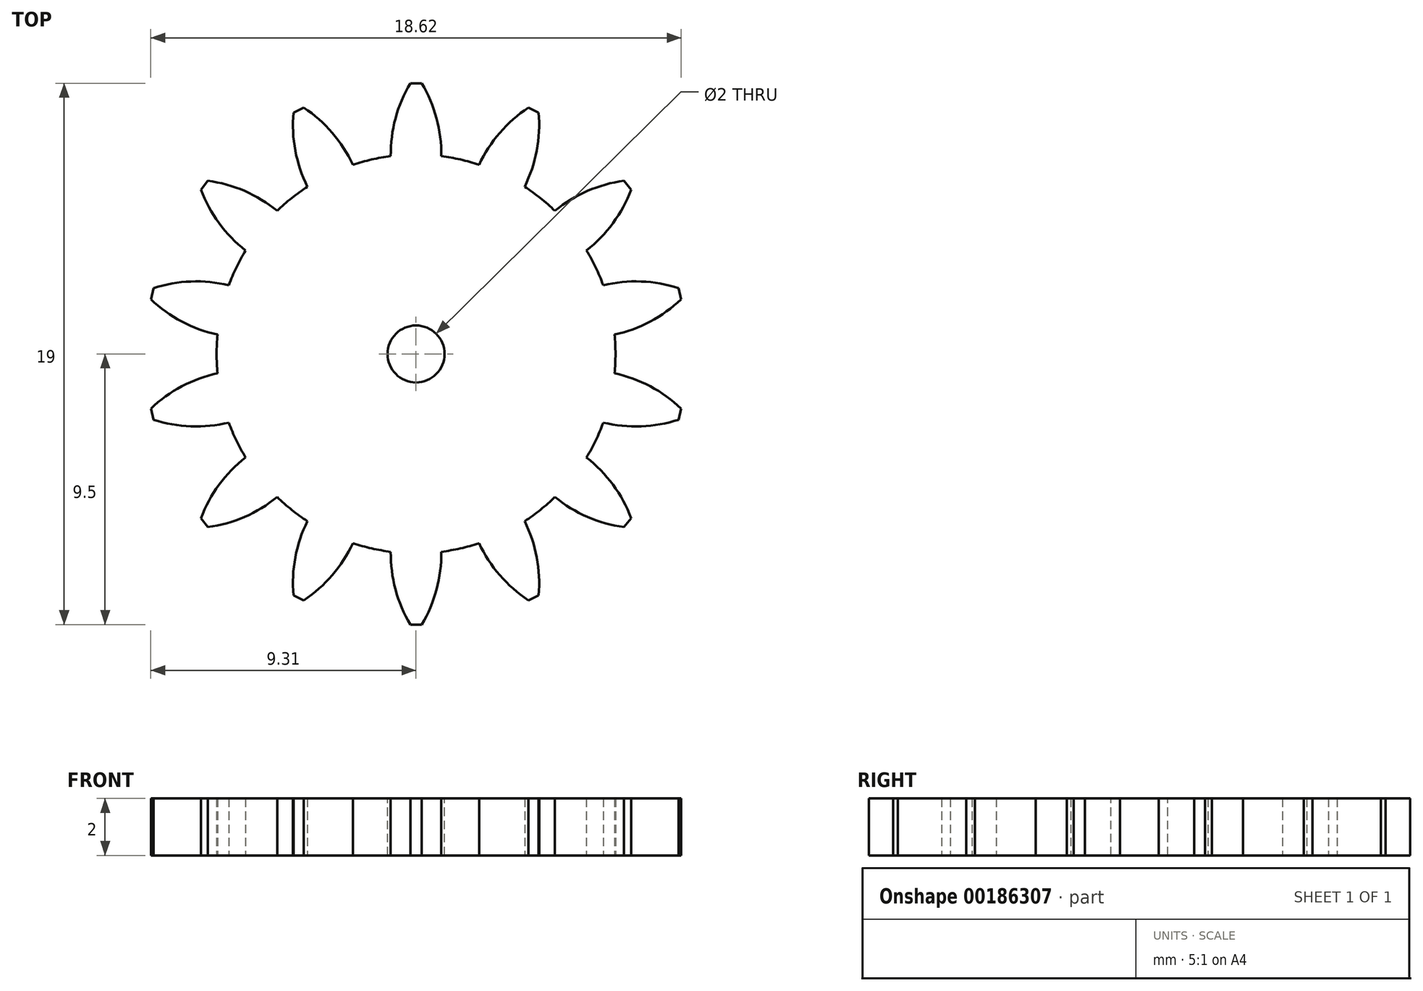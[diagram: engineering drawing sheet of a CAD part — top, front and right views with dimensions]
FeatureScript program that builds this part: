
annotation { "Feature Type Name" : "Feature", "Feature Type Description" : "" }
export const myFeature = defineFeature(function(context is Context, id is Id, definition is map)
    precondition{}
    {
        {
            var Q0;
            Q0=qCreatedBy(makeId("Top.planeOp"),FACE);
            var sketch = newSketch(context, id + "F0", { "sketchPlane" : qUnion([Q0])});
            skCircle(sketch, "E0", {"center": v(0, 0) * mm, "radius": 7 * mm});
            skLineSegment(sketch, "E1", {"start": v(0, 0) * mm, "end": v(0, 7) * mm, "construction": true});
            skArc(sketch, "E2", {"start": v(-0.2, 9.5) * mm, "mid": v(-0.72, 8.27) * mm, "end": v(-0.89, 6.94) * mm});
            skLineSegment(sketch, "E3", {"start": v(0, 9.5) * mm, "end": v(-0.2, 9.5) * mm});
            skLineSegment(sketch, "E4.MirrorCS", {"start": v(0, 9.5) * mm, "end": v(0.2, 9.5) * mm});
            skArc(sketch, "E5.MirrorCS", {"start": v(0.2, 9.5) * mm, "mid": v(0.72, 8.27) * mm, "end": v(0.89, 6.94) * mm});
            skArc(sketch, "E6.1.0", {"start": v(-3.94, 8.65) * mm, "mid": v(-2.94, 7.76) * mm, "end": v(-2.21, 6.64) * mm});
            skLineSegment(sketch, "E6.1.1", {"start": v(-4.12, 8.56) * mm, "end": v(-3.94, 8.65) * mm});
            skLineSegment(sketch, "E6.1.2", {"start": v(-4.12, 8.56) * mm, "end": v(-4.3, 8.47) * mm});
            skArc(sketch, "E6.1.3", {"start": v(-4.3, 8.47) * mm, "mid": v(-4.24, 7.14) * mm, "end": v(-3.81, 5.87) * mm});
            skArc(sketch, "E6.2.0", {"start": v(-7.3, 6.08) * mm, "mid": v(-6.02, 5.72) * mm, "end": v(-4.88, 5.02) * mm});
            skLineSegment(sketch, "E6.2.1", {"start": v(-7.43, 5.92) * mm, "end": v(-7.3, 6.08) * mm});
            skLineSegment(sketch, "E6.2.2", {"start": v(-7.43, 5.92) * mm, "end": v(-7.55, 5.77) * mm});
            skArc(sketch, "E6.2.3", {"start": v(-7.55, 5.77) * mm, "mid": v(-6.91, 4.6) * mm, "end": v(-5.98, 3.64) * mm});
            skArc(sketch, "E6.3.0", {"start": v(-9.22, 2.3) * mm, "mid": v(-7.9, 2.54) * mm, "end": v(-6.57, 2.41) * mm});
            skLineSegment(sketch, "E6.3.1", {"start": v(-9.26, 2.11) * mm, "end": v(-9.22, 2.3) * mm});
            skLineSegment(sketch, "E6.3.2", {"start": v(-9.26, 2.11) * mm, "end": v(-9.3, 1.92) * mm});
            skArc(sketch, "E6.3.3", {"start": v(-9.3, 1.92) * mm, "mid": v(-8.22, 1.14) * mm, "end": v(-6.97, 0.68) * mm});
            skArc(sketch, "E6.4.0", {"start": v(-9.3, -1.92) * mm, "mid": v(-8.22, -1.14) * mm, "end": v(-6.97, -0.68) * mm});
            skLineSegment(sketch, "E6.4.1", {"start": v(-9.26, -2.11) * mm, "end": v(-9.3, -1.92) * mm});
            skLineSegment(sketch, "E6.4.2", {"start": v(-9.26, -2.11) * mm, "end": v(-9.22, -2.3) * mm});
            skArc(sketch, "E6.4.3", {"start": v(-9.22, -2.3) * mm, "mid": v(-7.9, -2.54) * mm, "end": v(-6.57, -2.41) * mm});
            skArc(sketch, "E6.5.0", {"start": v(-7.55, -5.77) * mm, "mid": v(-6.91, -4.6) * mm, "end": v(-5.98, -3.64) * mm});
            skLineSegment(sketch, "E6.5.1", {"start": v(-7.43, -5.92) * mm, "end": v(-7.55, -5.77) * mm});
            skLineSegment(sketch, "E6.5.2", {"start": v(-7.43, -5.92) * mm, "end": v(-7.3, -6.08) * mm});
            skArc(sketch, "E6.5.3", {"start": v(-7.3, -6.08) * mm, "mid": v(-6.02, -5.72) * mm, "end": v(-4.88, -5.02) * mm});
            skArc(sketch, "E6.6.0", {"start": v(-4.3, -8.47) * mm, "mid": v(-4.24, -7.14) * mm, "end": v(-3.81, -5.87) * mm});
            skLineSegment(sketch, "E6.6.1", {"start": v(-4.12, -8.56) * mm, "end": v(-4.3, -8.47) * mm});
            skLineSegment(sketch, "E6.6.2", {"start": v(-4.12, -8.56) * mm, "end": v(-3.94, -8.65) * mm});
            skArc(sketch, "E6.6.3", {"start": v(-3.94, -8.65) * mm, "mid": v(-2.94, -7.76) * mm, "end": v(-2.21, -6.64) * mm});
            skArc(sketch, "E6.7.0", {"start": v(-0.2, -9.5) * mm, "mid": v(-0.72, -8.27) * mm, "end": v(-0.89, -6.94) * mm});
            skLineSegment(sketch, "E6.7.1", {"start": v(0, -9.5) * mm, "end": v(-0.2, -9.5) * mm});
            skLineSegment(sketch, "E6.7.2", {"start": v(0, -9.5) * mm, "end": v(0.2, -9.5) * mm});
            skArc(sketch, "E6.7.3", {"start": v(0.2, -9.5) * mm, "mid": v(0.72, -8.27) * mm, "end": v(0.89, -6.94) * mm});
            skArc(sketch, "E6.8.0", {"start": v(3.94, -8.65) * mm, "mid": v(2.94, -7.76) * mm, "end": v(2.21, -6.64) * mm});
            skLineSegment(sketch, "E6.8.1", {"start": v(4.12, -8.56) * mm, "end": v(3.94, -8.65) * mm});
            skLineSegment(sketch, "E6.8.2", {"start": v(4.12, -8.56) * mm, "end": v(4.3, -8.47) * mm});
            skArc(sketch, "E6.8.3", {"start": v(4.3, -8.47) * mm, "mid": v(4.24, -7.14) * mm, "end": v(3.81, -5.87) * mm});
            skArc(sketch, "E6.9.0", {"start": v(7.3, -6.08) * mm, "mid": v(6.02, -5.72) * mm, "end": v(4.88, -5.02) * mm});
            skLineSegment(sketch, "E6.9.1", {"start": v(7.43, -5.92) * mm, "end": v(7.3, -6.08) * mm});
            skLineSegment(sketch, "E6.9.2", {"start": v(7.43, -5.92) * mm, "end": v(7.55, -5.77) * mm});
            skArc(sketch, "E6.9.3", {"start": v(7.55, -5.77) * mm, "mid": v(6.91, -4.6) * mm, "end": v(5.98, -3.64) * mm});
            skArc(sketch, "E6.10.0", {"start": v(9.22, -2.3) * mm, "mid": v(7.9, -2.54) * mm, "end": v(6.57, -2.41) * mm});
            skLineSegment(sketch, "E6.10.1", {"start": v(9.26, -2.11) * mm, "end": v(9.22, -2.3) * mm});
            skLineSegment(sketch, "E6.10.2", {"start": v(9.26, -2.11) * mm, "end": v(9.3, -1.92) * mm});
            skArc(sketch, "E6.10.3", {"start": v(9.3, -1.92) * mm, "mid": v(8.22, -1.14) * mm, "end": v(6.97, -0.68) * mm});
            skArc(sketch, "E6.11.0", {"start": v(9.3, 1.92) * mm, "mid": v(8.22, 1.14) * mm, "end": v(6.97, 0.68) * mm});
            skLineSegment(sketch, "E6.11.1", {"start": v(9.26, 2.11) * mm, "end": v(9.3, 1.92) * mm});
            skLineSegment(sketch, "E6.11.2", {"start": v(9.26, 2.11) * mm, "end": v(9.22, 2.3) * mm});
            skArc(sketch, "E6.11.3", {"start": v(9.22, 2.3) * mm, "mid": v(7.9, 2.54) * mm, "end": v(6.57, 2.41) * mm});
            skArc(sketch, "E6.12.0", {"start": v(7.55, 5.77) * mm, "mid": v(6.91, 4.6) * mm, "end": v(5.98, 3.64) * mm});
            skLineSegment(sketch, "E6.12.1", {"start": v(7.43, 5.92) * mm, "end": v(7.55, 5.77) * mm});
            skLineSegment(sketch, "E6.12.2", {"start": v(7.43, 5.92) * mm, "end": v(7.3, 6.08) * mm});
            skArc(sketch, "E6.12.3", {"start": v(7.3, 6.08) * mm, "mid": v(6.02, 5.72) * mm, "end": v(4.88, 5.02) * mm});
            skArc(sketch, "E6.13.0", {"start": v(4.3, 8.47) * mm, "mid": v(4.24, 7.14) * mm, "end": v(3.81, 5.87) * mm});
            skLineSegment(sketch, "E6.13.1", {"start": v(4.12, 8.56) * mm, "end": v(4.3, 8.47) * mm});
            skLineSegment(sketch, "E6.13.2", {"start": v(4.12, 8.56) * mm, "end": v(3.94, 8.65) * mm});
            skArc(sketch, "E6.13.3", {"start": v(3.94, 8.65) * mm, "mid": v(2.94, 7.76) * mm, "end": v(2.21, 6.64) * mm});
            skSolve(sketch);
        }
        {
            var Q0;
            Q0=qSketchRegion(id+"F0",true);
            extrude(context, id + "F1", {"entities" : qUnion([Q0]), "depth" : 2 * mm});
        }
        {
            var Q0;
            Q0=makeQuery(id+"F1.opExtrude","CAP_FACE",FACE,{"disambiguationData":[OSD([sQuery(id+"F0.wireOp",EDGE,"E0"),sQuery(id+"F0.wireOp",EDGE,"E2"),sQuery(id+"F0.wireOp",EDGE,"E3"),sQuery(id+"F0.wireOp",EDGE,"E4.MirrorCS"),sQuery(id+"F0.wireOp",EDGE,"E5.MirrorCS"),sQuery(id+"F0.wireOp",EDGE,"E6.1.0"),sQuery(id+"F0.wireOp",EDGE,"E6.1.1"),sQuery(id+"F0.wireOp",EDGE,"E6.1.2"),sQuery(id+"F0.wireOp",EDGE,"E6.1.3"),sQuery(id+"F0.wireOp",EDGE,"E6.2.0"),sQuery(id+"F0.wireOp",EDGE,"E6.2.1"),sQuery(id+"F0.wireOp",EDGE,"E6.2.2"),sQuery(id+"F0.wireOp",EDGE,"E6.2.3"),sQuery(id+"F0.wireOp",EDGE,"E6.3.0"),sQuery(id+"F0.wireOp",EDGE,"E6.3.1"),sQuery(id+"F0.wireOp",EDGE,"E6.3.2"),sQuery(id+"F0.wireOp",EDGE,"E6.3.3"),sQuery(id+"F0.wireOp",EDGE,"E6.4.0"),sQuery(id+"F0.wireOp",EDGE,"E6.4.1"),sQuery(id+"F0.wireOp",EDGE,"E6.4.2"),sQuery(id+"F0.wireOp",EDGE,"E6.4.3"),sQuery(id+"F0.wireOp",EDGE,"E6.5.0"),sQuery(id+"F0.wireOp",EDGE,"E6.5.1"),sQuery(id+"F0.wireOp",EDGE,"E6.5.2"),sQuery(id+"F0.wireOp",EDGE,"E6.5.3"),sQuery(id+"F0.wireOp",EDGE,"E6.6.0"),sQuery(id+"F0.wireOp",EDGE,"E6.6.1"),sQuery(id+"F0.wireOp",EDGE,"E6.6.2"),sQuery(id+"F0.wireOp",EDGE,"E6.6.3"),sQuery(id+"F0.wireOp",EDGE,"E6.7.0"),sQuery(id+"F0.wireOp",EDGE,"E6.7.1"),sQuery(id+"F0.wireOp",EDGE,"E6.7.2"),sQuery(id+"F0.wireOp",EDGE,"E6.7.3"),sQuery(id+"F0.wireOp",EDGE,"E6.8.0"),sQuery(id+"F0.wireOp",EDGE,"E6.8.1"),sQuery(id+"F0.wireOp",EDGE,"E6.8.2"),sQuery(id+"F0.wireOp",EDGE,"E6.8.3"),sQuery(id+"F0.wireOp",EDGE,"E6.9.0"),sQuery(id+"F0.wireOp",EDGE,"E6.9.1"),sQuery(id+"F0.wireOp",EDGE,"E6.9.2"),sQuery(id+"F0.wireOp",EDGE,"E6.9.3"),sQuery(id+"F0.wireOp",EDGE,"E6.10.0"),sQuery(id+"F0.wireOp",EDGE,"E6.10.1"),sQuery(id+"F0.wireOp",EDGE,"E6.10.2"),sQuery(id+"F0.wireOp",EDGE,"E6.10.3"),sQuery(id+"F0.wireOp",EDGE,"E6.11.0"),sQuery(id+"F0.wireOp",EDGE,"E6.11.1"),sQuery(id+"F0.wireOp",EDGE,"E6.11.2"),sQuery(id+"F0.wireOp",EDGE,"E6.11.3"),sQuery(id+"F0.wireOp",EDGE,"E6.12.0"),sQuery(id+"F0.wireOp",EDGE,"E6.12.1"),sQuery(id+"F0.wireOp",EDGE,"E6.12.2"),sQuery(id+"F0.wireOp",EDGE,"E6.12.3"),sQuery(id+"F0.wireOp",EDGE,"E6.13.0"),sQuery(id+"F0.wireOp",EDGE,"E6.13.1"),sQuery(id+"F0.wireOp",EDGE,"E6.13.2"),sQuery(id+"F0.wireOp",EDGE,"E6.13.3"),sQuery(id+"F0.wireOp",EDGE,"E6.14.0"),sQuery(id+"F0.wireOp",EDGE,"E6.14.1"),sQuery(id+"F0.wireOp",EDGE,"E6.14.2"),sQuery(id+"F0.wireOp",EDGE,"E6.14.3"),sQuery(id+"F0.wireOp",EDGE,"E6.15.0"),sQuery(id+"F0.wireOp",EDGE,"E6.15.1"),sQuery(id+"F0.wireOp",EDGE,"E6.15.2"),sQuery(id+"F0.wireOp",EDGE,"E6.15.3")])],"isStart":false});
            var sketch = newSketch(context, id + "F2", { "sketchPlane" : qUnion([Q0])});
            skCircle(sketch, "E7", {"center": v(0, 0) * mm, "radius": 1 * mm});
            skSolve(sketch);
        }
        {
            var Q0;
            Q0=qSketchRegion(id+"F2",true);
            extrude(context, id + "F3", {"entities" : qUnion([Q0]), "operationType" : NewBodyOperationType.REMOVE, "oppositeDirection" : true, "depth" : 25 * mm});
        }
    });
